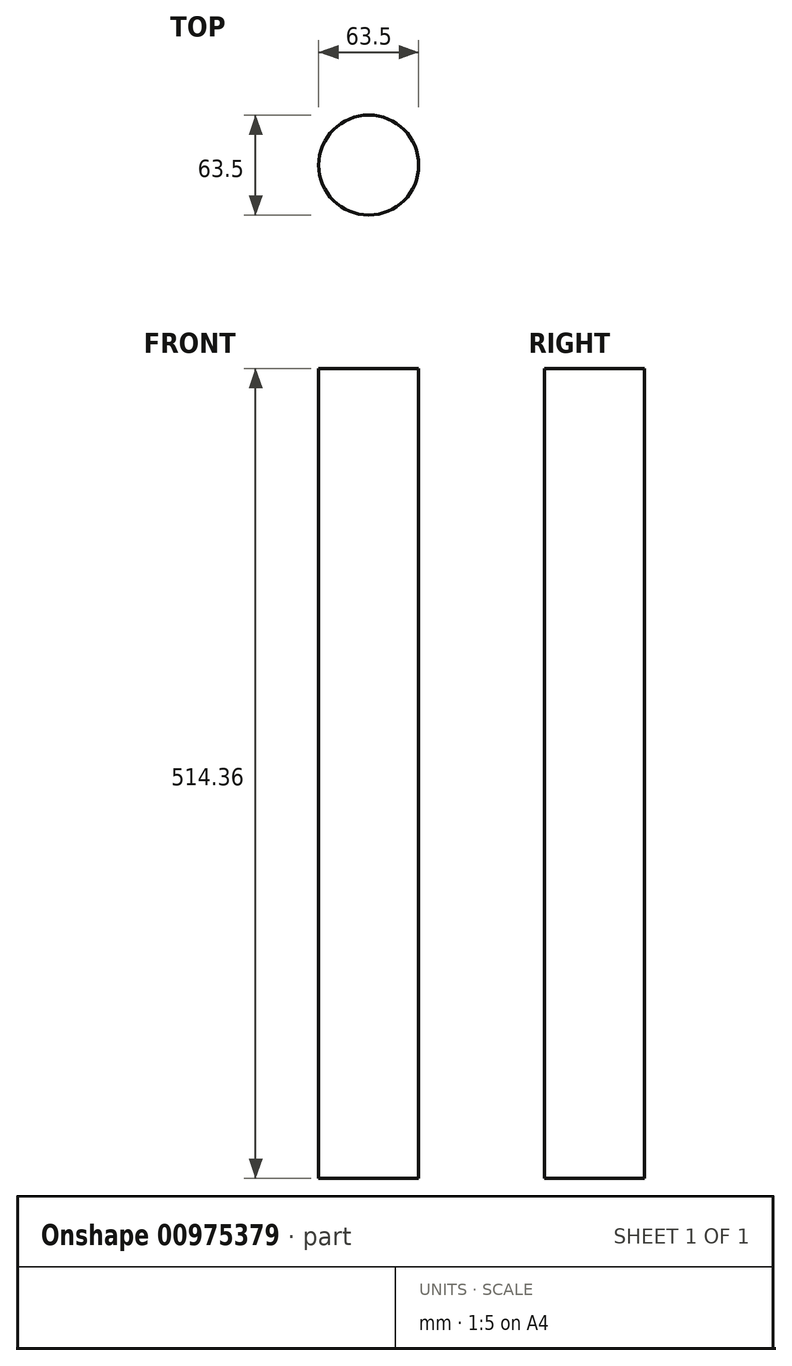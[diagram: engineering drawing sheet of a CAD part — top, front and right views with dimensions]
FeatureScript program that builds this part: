
annotation { "Feature Type Name" : "Feature", "Feature Type Description" : "" }
export const myFeature = defineFeature(function(context is Context, id is Id, definition is map)
    precondition{}
    {
        {
            var Q0;
            Q0=qCreatedBy(makeId("Top.planeOp"),FACE);
            var sketch = newSketch(context, id + "F0", { "sketchPlane" : qUnion([Q0])});
            skCircle(sketch, "E0", {"center": v(0, 0) * mm, "radius": 31.75 * mm});
            skSolve(sketch);
        }
        {
            var Q0;
            Q0=makeQuery(id+"F0.imprint","IMPRINT",FACE,{"disambiguationData":[TD([[makeQuery(id+"F0.imprint","IMPRINT",EDGE,{"derivedFrom":sQuery(id+"F0.wireOp",EDGE,"E0")}),1.0]])]});
            extrude(context, id + "F1", {"entities" : qUnion([Q0]), "endBound" : BoundingType.SYMMETRIC, "depth" : 514.35 * mm, "offsetDistance" : 25.4 * mm});
        }
    });
